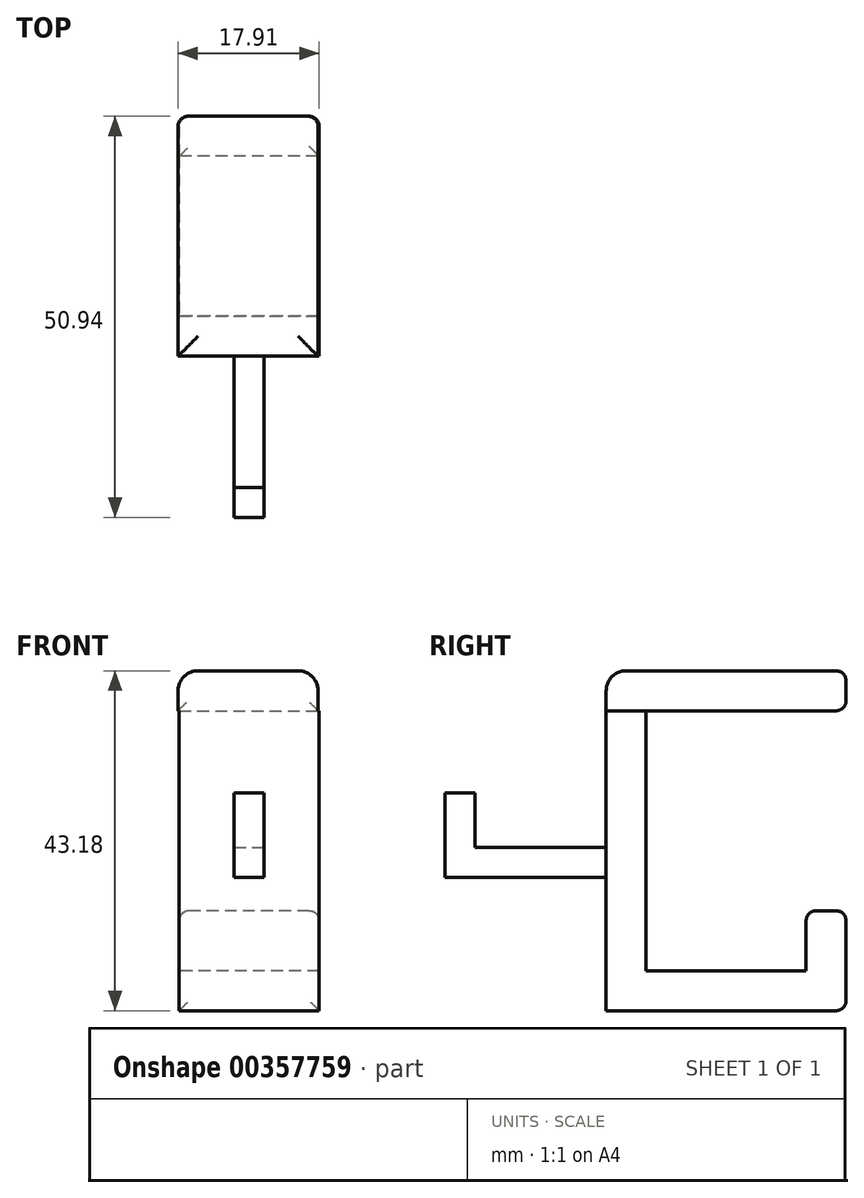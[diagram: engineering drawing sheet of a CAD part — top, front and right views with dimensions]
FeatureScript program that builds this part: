
annotation { "Feature Type Name" : "Feature", "Feature Type Description" : "" }
export const myFeature = defineFeature(function(context is Context, id is Id, definition is map)
    precondition{}
    {
        {
            var Q0;
            Q0=qCreatedBy(makeId("Top.planeOp"),FACE);
            cPlane(context, id + "F0", {"entities" : qUnion([Q0]), "cplaneType" : CPlaneType.OFFSET, "offset" : 25.4 * mm, "width" : 152.4 * mm, "height" : 152.4 * mm});
        }
        {
            var Q0;
            Q0=qCreatedBy(id+"F0.planeOp",FACE);
            var sketch = newSketch(context, id + "F1", { "sketchPlane" : qUnion([Q0])});
            skLineSegment(sketch, "E0.bottom", {"start": v(-10.21, 0) * mm, "end": v(7.57, 0) * mm});
            skLineSegment(sketch, "E0.top", {"start": v(-10.21, 30.48) * mm, "end": v(7.57, 30.48) * mm});
            skLineSegment(sketch, "E0.left", {"start": v(-10.21, 0) * mm, "end": v(-10.21, 30.48) * mm});
            skLineSegment(sketch, "E0.right", {"start": v(7.57, 0) * mm, "end": v(7.57, 30.48) * mm});
            skSolve(sketch);
        }
        {
            var Q0;
            Q0=makeQuery(id+"F1.imprint","IMPRINT",FACE,{"disambiguationData":[TD([[makeQuery(id+"F1.imprint","IMPRINT",EDGE,{"derivedFrom":sQuery(id+"F1.wireOp",EDGE,"E0.bottom")}),1.0]])]});
            extrude(context, id + "F2", {"entities" : qUnion([Q0]), "depth" : 5.08 * mm});
        }
        {
            var Q0;
            Q0=qCreatedBy(id+"F0.planeOp",FACE);
            var sketch = newSketch(context, id + "F3", { "sketchPlane" : qUnion([Q0])});
            skLineSegment(sketch, "E1.bottom", {"start": v(-10.08, 0) * mm, "end": v(7.7, 0) * mm});
            skLineSegment(sketch, "E1.top", {"start": v(-10.08, 5.08) * mm, "end": v(7.7, 5.08) * mm});
            skLineSegment(sketch, "E1.left", {"start": v(-10.08, 0) * mm, "end": v(-10.08, 5.08) * mm});
            skLineSegment(sketch, "E1.right", {"start": v(7.7, 0) * mm, "end": v(7.7, 5.08) * mm});
            skSolve(sketch);
        }
        {
            var Q0;
            Q0=makeQuery(id+"F3.imprint","IMPRINT",FACE,{"disambiguationData":[TD([[makeQuery(id+"F3.imprint","IMPRINT",EDGE,{"derivedFrom":sQuery(id+"F3.wireOp",EDGE,"E1.bottom")}),1.0]])]});
            extrude(context, id + "F4", {"entities" : qUnion([Q0]), "operationType" : NewBodyOperationType.ADD, "oppositeDirection" : true, "depth" : 38.1 * mm});
        }
        {
            var Q0;
            Q0=makeQuery(id+"F4.opExtrude","SWEPT_FACE",FACE,{"disambiguationData":[OSD([sQuery(id+"F3.wireOp",EDGE,"E1.top")])]});
            cPlane(context, id + "F5", {"entities" : qUnion([Q0]), "cplaneType" : CPlaneType.OFFSET, "offset" : 0 * mm, "width" : 152.4 * mm, "height" : 152.4 * mm});
        }
        {
            var Q0;
            Q0=qCreatedBy(id+"F5.planeOp",FACE);
            var sketch = newSketch(context, id + "F6", { "sketchPlane" : qUnion([Q0])});
            skLineSegment(sketch, "E2.0.0", {"start": v(10.08, 25.4) * mm, "end": v(-7.57, 25.4) * mm});
            skLineSegment(sketch, "E2.0.1", {"start": v(-7.57, 25.4) * mm, "end": v(-7.7, 25.4) * mm});
            skLineSegment(sketch, "E2.0.2", {"start": v(-7.7, 25.4) * mm, "end": v(-7.7, -12.7) * mm});
            skLineSegment(sketch, "E2.0.3", {"start": v(-7.7, -12.7) * mm, "end": v(10.08, -12.7) * mm});
            skLineSegment(sketch, "E2.0.4", {"start": v(10.08, -12.7) * mm, "end": v(10.08, 25.4) * mm});
            skLineSegment(sketch, "E3.left", {"start": v(-7.7, -12.7) * mm, "end": v(-7.7, -12.7) * mm});
            skLineSegment(sketch, "E3.right", {"start": v(10.08, -12.7) * mm, "end": v(10.08, -12.7) * mm});
            skLineSegment(sketch, "E4.top", {"start": v(-7.7, -7.62) * mm, "end": v(10.08, -7.62) * mm});
            skLineSegment(sketch, "E4.left", {"start": v(-7.7, -12.7) * mm, "end": v(-7.7, -7.62) * mm});
            skLineSegment(sketch, "E4.right", {"start": v(10.08, -12.7) * mm, "end": v(10.08, -7.62) * mm});
            skSolve(sketch);
        }
        {
            var Q0;
            Q0=makeQuery(id+"F6.imprint","IMPRINT",FACE,{"disambiguationData":[TD([[makeQuery(id+"F6.imprint","IMPRINT",EDGE,{"derivedFrom":sQuery(id+"F6.wireOp",EDGE,"E2.0.3")}),1.0]])]});
            extrude(context, id + "F7", {"entities" : qUnion([Q0]), "operationType" : NewBodyOperationType.ADD, "depth" : 25.4 * mm});
        }
        {
            var Q0;
            Q0=makeQuery(id+"F7.opExtrude","SWEPT_FACE",FACE,{"disambiguationData":[OSD([sQuery(id+"F6.wireOp",EDGE,"E4.top")])]});
            cPlane(context, id + "F8", {"entities" : qUnion([Q0]), "cplaneType" : CPlaneType.OFFSET, "offset" : 0 * mm, "width" : 152.4 * mm, "height" : 152.4 * mm});
        }
        {
            var Q0;
            Q0=qCreatedBy(id+"F8.planeOp",FACE);
            var sketch = newSketch(context, id + "F9", { "sketchPlane" : qUnion([Q0])});
            skLineSegment(sketch, "E5.0.0", {"start": v(-10.08, 5.08) * mm, "end": v(7.7, 5.08) * mm});
            skLineSegment(sketch, "E5.0.1", {"start": v(7.7, 5.08) * mm, "end": v(7.7, 30.48) * mm});
            skLineSegment(sketch, "E5.0.2", {"start": v(7.7, 30.48) * mm, "end": v(-10.08, 30.48) * mm});
            skLineSegment(sketch, "E5.0.3", {"start": v(-10.08, 30.48) * mm, "end": v(-10.08, 5.08) * mm});
            skLineSegment(sketch, "E6.top", {"start": v(7.7, 25.4) * mm, "end": v(-10.08, 25.4) * mm});
            skLineSegment(sketch, "E6.left", {"start": v(7.7, 30.48) * mm, "end": v(7.7, 25.4) * mm});
            skLineSegment(sketch, "E6.right", {"start": v(-10.08, 30.48) * mm, "end": v(-10.08, 25.4) * mm});
            skSolve(sketch);
        }
        {
            var Q0;
            Q0=makeQuery(id+"F9.imprint","IMPRINT",FACE,{"disambiguationData":[TD([[makeQuery(id+"F9.imprint","IMPRINT",EDGE,{"derivedFrom":sQuery(id+"F9.wireOp",EDGE,"E5.0.2")}),1.0]])]});
            extrude(context, id + "F10", {"entities" : qUnion([Q0]), "operationType" : NewBodyOperationType.ADD, "depth" : 7.62 * mm});
        }
        {
            var Q0;
            Q0=makeQuery(id+"F10.opExtrude","CAP_FACE",FACE,{"disambiguationData":[OSD([sQuery(id+"F9.wireOp",EDGE,"E5.0.2"),sQuery(id+"F9.wireOp",EDGE,"E6.top"),sQuery(id+"F9.wireOp",EDGE,"E6.left"),sQuery(id+"F9.wireOp",EDGE,"E6.right")])],"isStart":false});
            var Q1;
            Q1=makeQuery(id+"F10.boolean.opBoolean","MERGE",FACE,{"derivedFrom":[makeQuery(id+"F7.opExtrude","CAP_FACE",FACE,{"disambiguationData":[OSD([sQuery(id+"F6.wireOp",EDGE,"E2.0.3"),sQuery(id+"F6.wireOp",EDGE,"E4.top"),sQuery(id+"F6.wireOp",EDGE,"E4.left"),sQuery(id+"F6.wireOp",EDGE,"E4.right")])],"isStart":false}),makeQuery(id+"F10.opExtrude","SWEPT_FACE",FACE,{"disambiguationData":[OSD([sQuery(id+"F9.wireOp",EDGE,"E5.0.2")])]})]});
            fillet(context, id + "F11", {"entities" : qUnion([Q0, Q1]), "radius" : 1.27 * mm, "tangentPropagation" : true, "allowEdgeOverflow" : false});
        }
        {
            var Q0;
            Q0=makeQuery(id+"F2.opExtrude","SWEPT_FACE",FACE,{"disambiguationData":[OSD([sQuery(id+"F1.wireOp",EDGE,"E0.top")])]});
            fillet(context, id + "F12", {"entities" : qUnion([Q0]), "radius" : 1.27 * mm, "tangentPropagation" : true, "allowEdgeOverflow" : false});
        }
        {
            var Q0;
            Q0=makeQuery(id+"F2.opExtrude","CAP_FACE",FACE,{"disambiguationData":[OSD([sQuery(id+"F1.wireOp",EDGE,"E0.bottom"),sQuery(id+"F1.wireOp",EDGE,"E0.top"),sQuery(id+"F1.wireOp",EDGE,"E0.left"),sQuery(id+"F1.wireOp",EDGE,"E0.right")])],"isStart":false});
            fillet(context, id + "F13", {"entities" : qUnion([Q0]), "radius" : 2.54 * mm, "tangentPropagation" : true, "allowEdgeOverflow" : false});
        }
        {
            var Q0;
            Q0=makeQuery(id+"F10.boolean.opBoolean","MERGE",FACE,{"derivedFrom":[makeQuery(id+"F7.boolean.opBoolean","MERGE",FACE,{"derivedFrom":[makeQuery(id+"F4.opExtrude","SWEPT_FACE",FACE,{"disambiguationData":[OSD([sQuery(id+"F3.wireOp",EDGE,"E1.right")])]}),makeQuery(id+"F7.opExtrude","SWEPT_FACE",FACE,{"disambiguationData":[OSD([sQuery(id+"F6.wireOp",EDGE,"E4.left")])]})]}),makeQuery(id+"F10.opExtrude","SWEPT_FACE",FACE,{"disambiguationData":[OSD([sQuery(id+"F9.wireOp",EDGE,"E6.left")])]})]});
            cPlane(context, id + "F14", {"entities" : qUnion([Q0]), "cplaneType" : CPlaneType.OFFSET, "offset" : 8.9 * mm, "oppositeDirection" : true, "width" : 152.4 * mm, "height" : 152.4 * mm});
        }
        {
            var Q0;
            Q0=qCreatedBy(id+"F14.planeOp",FACE);
            var sketch = newSketch(context, id + "F15", { "sketchPlane" : qUnion([Q0])});
            skLineSegment(sketch, "E7.0.0", {"start": v(29.21, -12.7) * mm, "end": v(29.21, -1.27) * mm});
            skLineSegment(sketch, "E7.0.1", {"start": v(29.21, -1.27) * mm, "end": v(25.4, -1.27) * mm});
            skLineSegment(sketch, "E7.0.2", {"start": v(25.4, -1.27) * mm, "end": v(25.4, -7.62) * mm});
            skLineSegment(sketch, "E7.0.3", {"start": v(25.4, -7.62) * mm, "end": v(5.08, -7.62) * mm});
            skLineSegment(sketch, "E7.0.4", {"start": v(5.08, -7.62) * mm, "end": v(5.08, 25.4) * mm});
            skLineSegment(sketch, "E7.0.5", {"start": v(5.08, 25.4) * mm, "end": v(0, 25.4) * mm});
            skLineSegment(sketch, "E7.0.6", {"start": v(0, 25.4) * mm, "end": v(0, -12.7) * mm});
            skLineSegment(sketch, "E7.0.7", {"start": v(0, -12.7) * mm, "end": v(29.21, -12.7) * mm});
            skLineSegment(sketch, "E8", {"start": v(0, 4.24) * mm, "end": v(-20.46, 4.24) * mm});
            skLineSegment(sketch, "E9", {"start": v(-20.46, 4.24) * mm, "end": v(-20.46, 14.93) * mm});
            skLineSegment(sketch, "E10", {"start": v(-20.46, 14.93) * mm, "end": v(-16.65, 14.93) * mm});
            skLineSegment(sketch, "E11", {"start": v(-16.65, 14.93) * mm, "end": v(-16.65, 8.05) * mm});
            skLineSegment(sketch, "E12", {"start": v(-16.65, 8.05) * mm, "end": v(0, 8.05) * mm});
            skLineSegment(sketch, "E13", {"start": v(0, 8.05) * mm, "end": v(0, 4.24) * mm});
            skSolve(sketch);
        }
        {
            var Q0;
            Q0=makeQuery(id+"F15.imprint","IMPRINT",FACE,{"disambiguationData":[TD([[makeQuery(id+"F15.imprint","IMPRINT",EDGE,{"derivedFrom":sQuery(id+"F15.wireOp",EDGE,"E8")}),-1.0]])]});
            extrude(context, id + "F16", {"entities" : qUnion([Q0]), "operationType" : NewBodyOperationType.ADD, "oppositeDirection" : true, "depth" : 3.8 * mm, "symmetric" : true});
        }
    });
